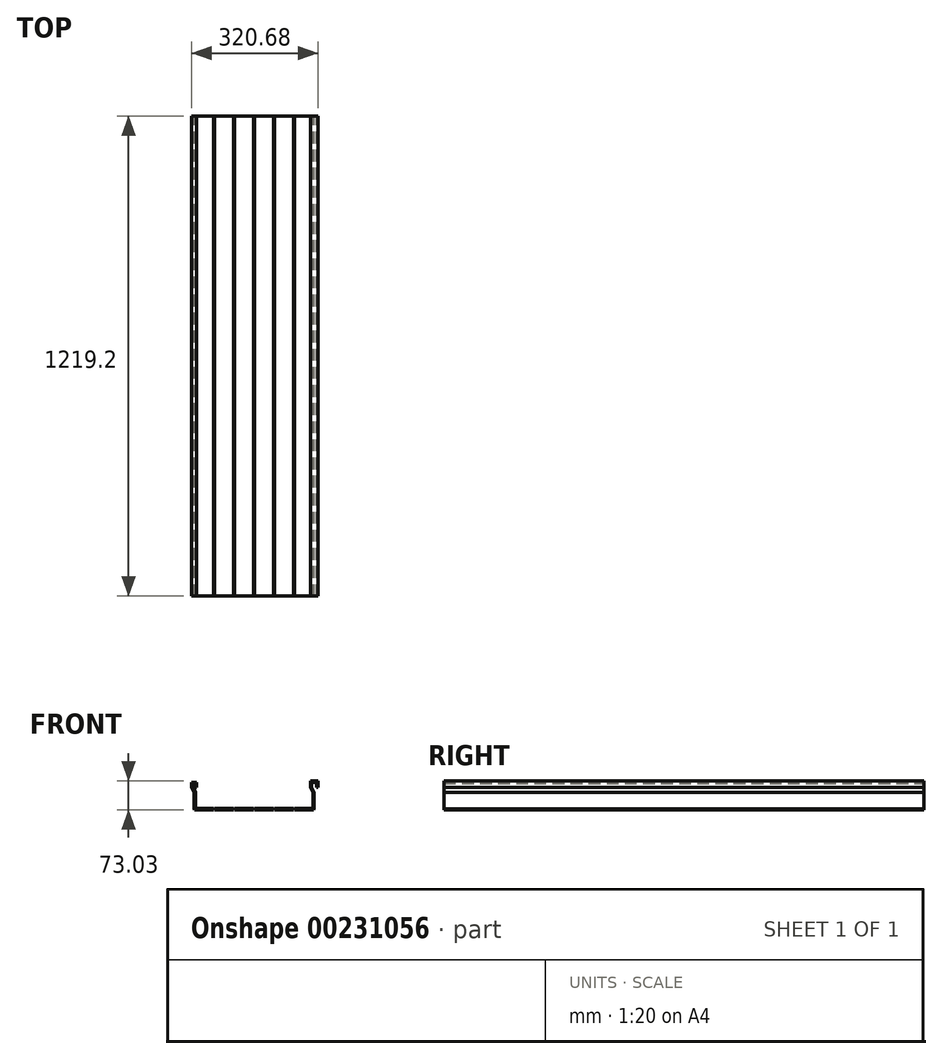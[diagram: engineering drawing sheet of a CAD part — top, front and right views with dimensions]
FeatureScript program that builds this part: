
annotation { "Feature Type Name" : "Feature", "Feature Type Description" : "" }
export const myFeature = defineFeature(function(context is Context, id is Id, definition is map)
    precondition{}
    {
        {
            var Q0;
            Q0=qCreatedBy(makeId("Front.planeOp"),FACE);
            var sketch = newSketch(context, id + "F0", { "sketchPlane" : qUnion([Q0])});
            skLineSegment(sketch, "E0", {"start": v(12.7, 57.15) * mm, "end": v(12.7, 69.85) * mm});
            skLineSegment(sketch, "E1", {"start": v(12.7, 69.85) * mm, "end": v(0, 69.85) * mm});
            skLineSegment(sketch, "E2", {"start": v(0, 69.85) * mm, "end": v(0, 57.15) * mm});
            skLineSegment(sketch, "E3", {"start": v(0, 57.15) * mm, "end": v(6.35, 44.45) * mm});
            skLineSegment(sketch, "E4", {"start": v(6.35, 44.45) * mm, "end": v(6.35, 1.59) * mm});
            skLineSegment(sketch, "E5", {"start": v(311.15, 1.59) * mm, "end": v(311.15, 44.45) * mm});
            skLineSegment(sketch, "E6", {"start": v(311.15, 44.45) * mm, "end": v(304.8, 57.15) * mm});
            skLineSegment(sketch, "E7", {"start": v(304.8, 57.15) * mm, "end": v(304.8, 69.85) * mm});
            skLineSegment(sketch, "E8", {"start": v(304.8, 69.85) * mm, "end": v(317.5, 69.85) * mm});
            skLineSegment(sketch, "E9", {"start": v(317.5, 69.85) * mm, "end": v(317.5, 57.15) * mm});
            skLineSegment(sketch, "E10.0", {"start": v(320.68, 73.03) * mm, "end": v(320.68, 57.15) * mm});
            skLineSegment(sketch, "E10.1", {"start": v(3.17, 57.9) * mm, "end": v(9.53, 45.2) * mm});
            skLineSegment(sketch, "E10.2", {"start": v(3.17, 66.68) * mm, "end": v(3.18, 57.9) * mm});
            skLineSegment(sketch, "E10.3", {"start": v(9.53, 66.68) * mm, "end": v(3.18, 66.68) * mm});
            skLineSegment(sketch, "E10.4", {"start": v(9.53, 57.15) * mm, "end": v(9.53, 66.68) * mm});
            skLineSegment(sketch, "E10.5", {"start": v(9.53, 45.2) * mm, "end": v(9.53, 3.18) * mm});
            skLineSegment(sketch, "E10.6", {"start": v(9.53, 3.18) * mm, "end": v(55.56, 3.18) * mm});
            skLineSegment(sketch, "E10.7", {"start": v(307.98, 3.18) * mm, "end": v(307.98, 43.7) * mm});
            skLineSegment(sketch, "E10.8", {"start": v(307.98, 43.7) * mm, "end": v(301.63, 56.4) * mm});
            skLineSegment(sketch, "E10.9", {"start": v(301.63, 56.4) * mm, "end": v(301.63, 73.03) * mm});
            skLineSegment(sketch, "E10.10", {"start": v(301.63, 73.03) * mm, "end": v(320.68, 73.03) * mm});
            skLineSegment(sketch, "E11", {"start": v(317.5, 57.15) * mm, "end": v(320.68, 57.15) * mm});
            skLineSegment(sketch, "E12", {"start": v(9.53, 57.15) * mm, "end": v(12.7, 57.15) * mm});
            skLineSegment(sketch, "E13", {"start": v(6.35, 1.59) * mm, "end": v(7.94, 0) * mm});
            skLineSegment(sketch, "E14", {"start": v(55.56, 0) * mm, "end": v(57.15, 1.59) * mm});
            skLineSegment(sketch, "E15", {"start": v(57.15, 1.59) * mm, "end": v(58.74, 0) * mm});
            skLineSegment(sketch, "E16.0.1.0", {"start": v(57.15, 4.76) * mm, "end": v(58.74, 3.18) * mm});
            skLineSegment(sketch, "E16.0.1.1", {"start": v(55.56, 3.17) * mm, "end": v(57.15, 4.76) * mm});
            skLineSegment(sketch, "E16.1.0.0", {"start": v(107.95, 1.59) * mm, "end": v(109.54, 0) * mm});
            skLineSegment(sketch, "E16.1.0.1", {"start": v(106.36, 0) * mm, "end": v(107.95, 1.59) * mm});
            skLineSegment(sketch, "E16.1.1.0", {"start": v(107.95, 4.76) * mm, "end": v(109.54, 3.18) * mm});
            skLineSegment(sketch, "E16.1.1.1", {"start": v(106.36, 3.17) * mm, "end": v(107.95, 4.76) * mm});
            skLineSegment(sketch, "E16.2.0.0", {"start": v(158.75, 1.59) * mm, "end": v(160.34, 0) * mm});
            skLineSegment(sketch, "E16.2.0.1", {"start": v(157.16, 0) * mm, "end": v(158.75, 1.59) * mm});
            skLineSegment(sketch, "E16.2.1.0", {"start": v(158.75, 4.76) * mm, "end": v(160.34, 3.18) * mm});
            skLineSegment(sketch, "E16.2.1.1", {"start": v(157.16, 3.18) * mm, "end": v(158.75, 4.76) * mm});
            skLineSegment(sketch, "E16.3.0.0", {"start": v(209.55, 1.59) * mm, "end": v(211.14, 0) * mm});
            skLineSegment(sketch, "E16.3.0.1", {"start": v(207.96, 0) * mm, "end": v(209.55, 1.59) * mm});
            skLineSegment(sketch, "E16.3.1.0", {"start": v(209.55, 4.76) * mm, "end": v(211.14, 3.17) * mm});
            skLineSegment(sketch, "E16.3.1.1", {"start": v(207.96, 3.18) * mm, "end": v(209.55, 4.76) * mm});
            skLineSegment(sketch, "E16.4.0.0", {"start": v(260.35, 1.59) * mm, "end": v(261.94, 0) * mm});
            skLineSegment(sketch, "E16.4.0.1", {"start": v(258.76, 0) * mm, "end": v(260.35, 1.59) * mm});
            skLineSegment(sketch, "E16.4.1.0", {"start": v(260.35, 4.76) * mm, "end": v(261.94, 3.17) * mm});
            skLineSegment(sketch, "E16.4.1.1", {"start": v(258.76, 3.18) * mm, "end": v(260.35, 4.76) * mm});
            skLineSegment(sketch, "E17", {"start": v(7.94, 0) * mm, "end": v(55.56, 0) * mm});
            skLineSegment(sketch, "E18", {"start": v(58.74, 0) * mm, "end": v(106.36, 0) * mm});
            skLineSegment(sketch, "E19", {"start": v(109.54, 0) * mm, "end": v(157.16, 0) * mm});
            skLineSegment(sketch, "E20", {"start": v(160.34, 0) * mm, "end": v(207.96, 0) * mm});
            skLineSegment(sketch, "E21", {"start": v(211.14, 0) * mm, "end": v(258.76, 0) * mm});
            skLineSegment(sketch, "E22", {"start": v(261.94, 0) * mm, "end": v(309.56, 0) * mm});
            skLineSegment(sketch, "E23.trimOffspring", {"start": v(261.94, 3.18) * mm, "end": v(307.98, 3.18) * mm});
            skLineSegment(sketch, "E24.trimOffspring", {"start": v(211.14, 3.18) * mm, "end": v(258.76, 3.18) * mm});
            skLineSegment(sketch, "E25.trimOffspring", {"start": v(160.34, 3.18) * mm, "end": v(207.96, 3.18) * mm});
            skLineSegment(sketch, "E26.trimOffspring", {"start": v(109.54, 3.18) * mm, "end": v(157.16, 3.18) * mm});
            skLineSegment(sketch, "E27.trimOffspring", {"start": v(58.74, 3.18) * mm, "end": v(106.36, 3.18) * mm});
            skLineSegment(sketch, "E28", {"start": v(311.15, 1.59) * mm, "end": v(309.56, 0) * mm});
            skSolve(sketch);
        }
        {
            var Q0;
            Q0 = qSketchRegion(id + "F0", true);
            extrude(context, id + "F1", {"entities" : qUnion([Q0]), "depth" : 1219.2 * mm});
        }
    });
